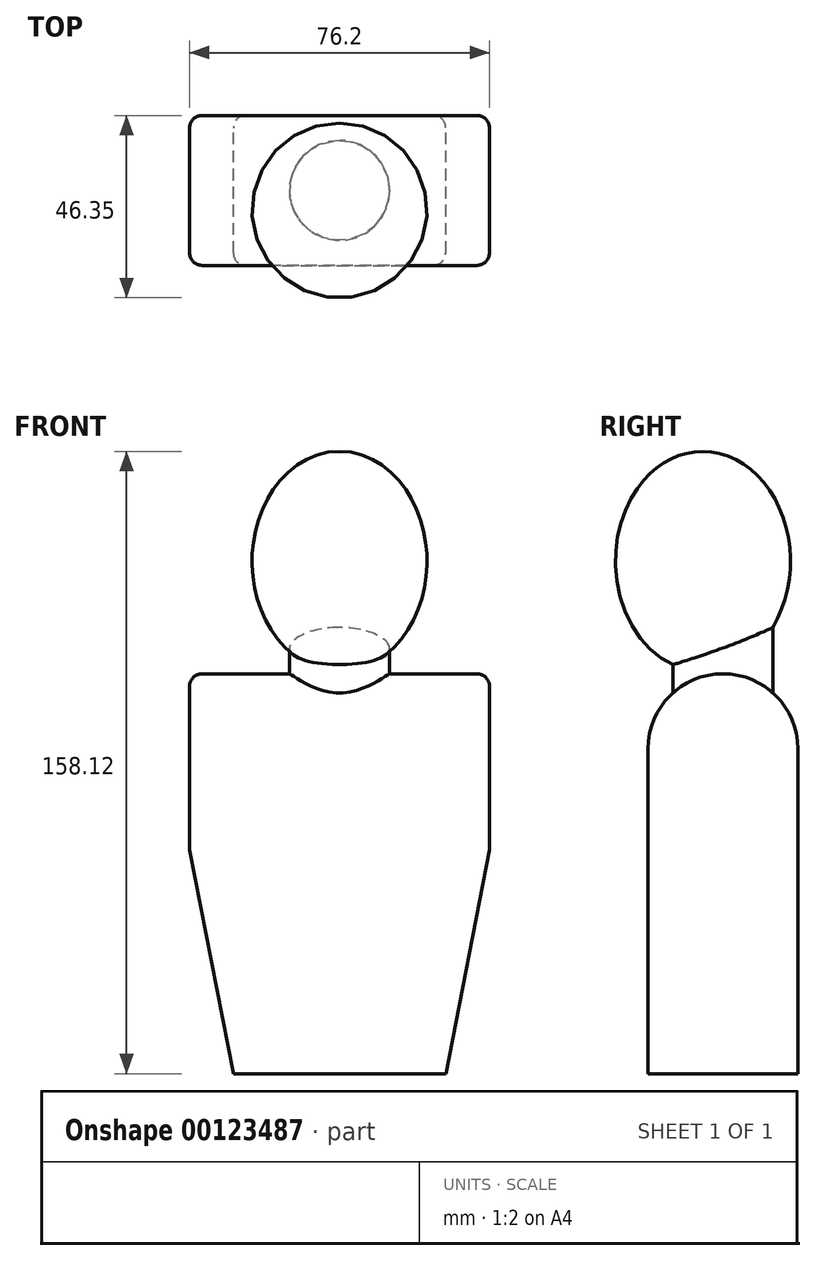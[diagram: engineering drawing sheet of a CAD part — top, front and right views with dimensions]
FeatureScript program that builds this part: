
annotation { "Feature Type Name" : "Feature", "Feature Type Description" : "" }
export const myFeature = defineFeature(function(context is Context, id is Id, definition is map)
    precondition{}
    {
        {
            var Q0;
            Q0=qCreatedBy(makeId("Front.planeOp"),FACE);
            var sketch = newSketch(context, id + "F0", { "sketchPlane" : qUnion([Q0])});
            skLineSegment(sketch, "E0", {"start": v(-26.99, 0) * mm, "end": v(26.99, 0) * mm});
            skLineSegment(sketch, "E1", {"start": v(26.99, 0) * mm, "end": v(38.1, 57.15) * mm});
            skLineSegment(sketch, "E2", {"start": v(38.1, 57.15) * mm, "end": v(38.1, 101.6) * mm});
            skLineSegment(sketch, "E3", {"start": v(38.1, 101.6) * mm, "end": v(-38.1, 101.6) * mm});
            skLineSegment(sketch, "E4", {"start": v(-38.1, 101.6) * mm, "end": v(-38.1, 57.15) * mm});
            skLineSegment(sketch, "E5", {"start": v(-38.1, 57.15) * mm, "end": v(-26.99, 0) * mm});
            skLineSegment(sketch, "E6", {"start": v(0, 0) * mm, "end": v(0, 101.6) * mm, "construction": true});
            skSolve(sketch);
        }
        {
            var Q0;
            Q0=qSketchRegion(id+"F0",true);
            extrude(context, id + "F1", {"entities" : qUnion([Q0]), "endBound" : BoundingType.SYMMETRIC, "depth" : 38.1 * mm});
        }
        {
            var Q0;
            Q0=makeQuery(id+"F1.opExtrude","CAP_EDGE",EDGE,{"disambiguationData":[OSD([sQuery(id+"F0.wireOp",EDGE,"E3")])],"isStart":false});
            var Q1;
            Q1=makeQuery(id+"F1.opExtrude","CAP_EDGE",EDGE,{"disambiguationData":[OSD([sQuery(id+"F0.wireOp",EDGE,"E3")])],"isStart":true});
            fillet(context, id + "F2", {"entities" : qUnion([Q0, Q1]), "radius" : 19.05 * mm, "tangentPropagation" : true, "allowEdgeOverflow" : false});
        }
        {
            var Q0;
            Q0=qCreatedBy(makeId("Front.planeOp"),FACE);
            var sketch = newSketch(context, id + "F3", { "sketchPlane" : qUnion([Q0])});
            skLineSegment(sketch, "E7.bottom", {"start": v(0, 82.55) * mm, "end": v(12.7, 82.55) * mm});
            skLineSegment(sketch, "E7.top", {"start": v(0, 120.65) * mm, "end": v(12.7, 120.65) * mm});
            skLineSegment(sketch, "E7.left", {"start": v(0, 82.55) * mm, "end": v(0, 120.65) * mm});
            skLineSegment(sketch, "E7.right", {"start": v(12.7, 82.55) * mm, "end": v(12.7, 120.65) * mm});
            skLineSegment(sketch, "E8", {"start": v(0, 82.55) * mm, "end": v(0, 0) * mm, "construction": true});
            skSolve(sketch);
        }
        {
            var Q0;
            Q0=qSketchRegion(id+"F3",true);
            var Q1;
            Q1=sQuery(id+"F3.wireOp",EDGE,"E8");
            revolve(context, id + "F4", {"operationType" : NewBodyOperationType.ADD, "entities" : qUnion([Q0]), "axis" : qUnion([Q1]), "revolveType" : RevolveType.FULL});
        }
        {
            var Q0;
            Q0=qCreatedBy(makeId("Right.planeOp"),FACE);
            var sketch = newSketch(context, id + "F5", { "sketchPlane" : qUnion([Q0])});
            skLineSegment(sketch, "E9", {"start": v(-5.08, 102.24) * mm, "end": v(-5.08, 158.12) * mm});
            skEllipticalArc(sketch, "E10", {});
            skLineSegment(sketch, "E11", {"start": v(-5.08, 102.24) * mm, "end": v(-5.08, 8.32) * mm, "construction": true});
            skLineSegment(sketch, "E12", {"start": v(-5.08, 130.18) * mm, "end": v(17.14, 130.18) * mm, "construction": true});
            const initialGuessF5  = {"E10": [-0.00508, 0.130175, 0, 1, 0.02794, 0.022225, 3.141592653589793, 0]};
            skSetInitialGuess(sketch, initialGuessF5);
            skSolve(sketch);
        }
        {
            var Q0;
            Q0=qSketchRegion(id+"F5",true);
            var Q1;
            Q1=sQuery(id+"F5.wireOp",EDGE,"E11");
            revolve(context, id + "F6", {"operationType" : NewBodyOperationType.ADD, "entities" : qUnion([Q0]), "axis" : qUnion([Q1]), "revolveType" : RevolveType.FULL});
        }
        {
            var Q0;
            Q0=makeQuery(id+"F1.opExtrude","SWEPT_EDGE",EDGE,{"disambiguationData":[OSD([sQuery(id+"F0.wireOp",EDGE,"E4"),sQuery(id+"F0.wireOp",EDGE,"E5")])]});
            var Q1;
            Q1=makeQuery(id+"F1.opExtrude","SWEPT_EDGE",EDGE,{"disambiguationData":[OSD([sQuery(id+"F0.wireOp",EDGE,"E1"),sQuery(id+"F0.wireOp",EDGE,"E2")])]});
            fillet(context, id + "F7", {"entities" : qUnion([Q0, Q1]), "radius" : 3.17 * mm, "tangentPropagation" : true, "allowEdgeOverflow" : false});
        }
        {
            var Q0;
            Q0=makeQuery(id+"F1.opExtrude","CAP_EDGE",EDGE,{"disambiguationData":[OSD([sQuery(id+"F0.wireOp",EDGE,"E1")])],"isStart":false});
            var Q1;
            Q1=makeQuery(id+"F1.opExtrude","CAP_EDGE",EDGE,{"disambiguationData":[OSD([sQuery(id+"F0.wireOp",EDGE,"E5")])],"isStart":false});
            fillet(context, id + "F8", {"entities" : qUnion([Q0, Q1]), "radius" : 3.17 * mm, "tangentPropagation" : true, "allowEdgeOverflow" : false});
        }
    });
